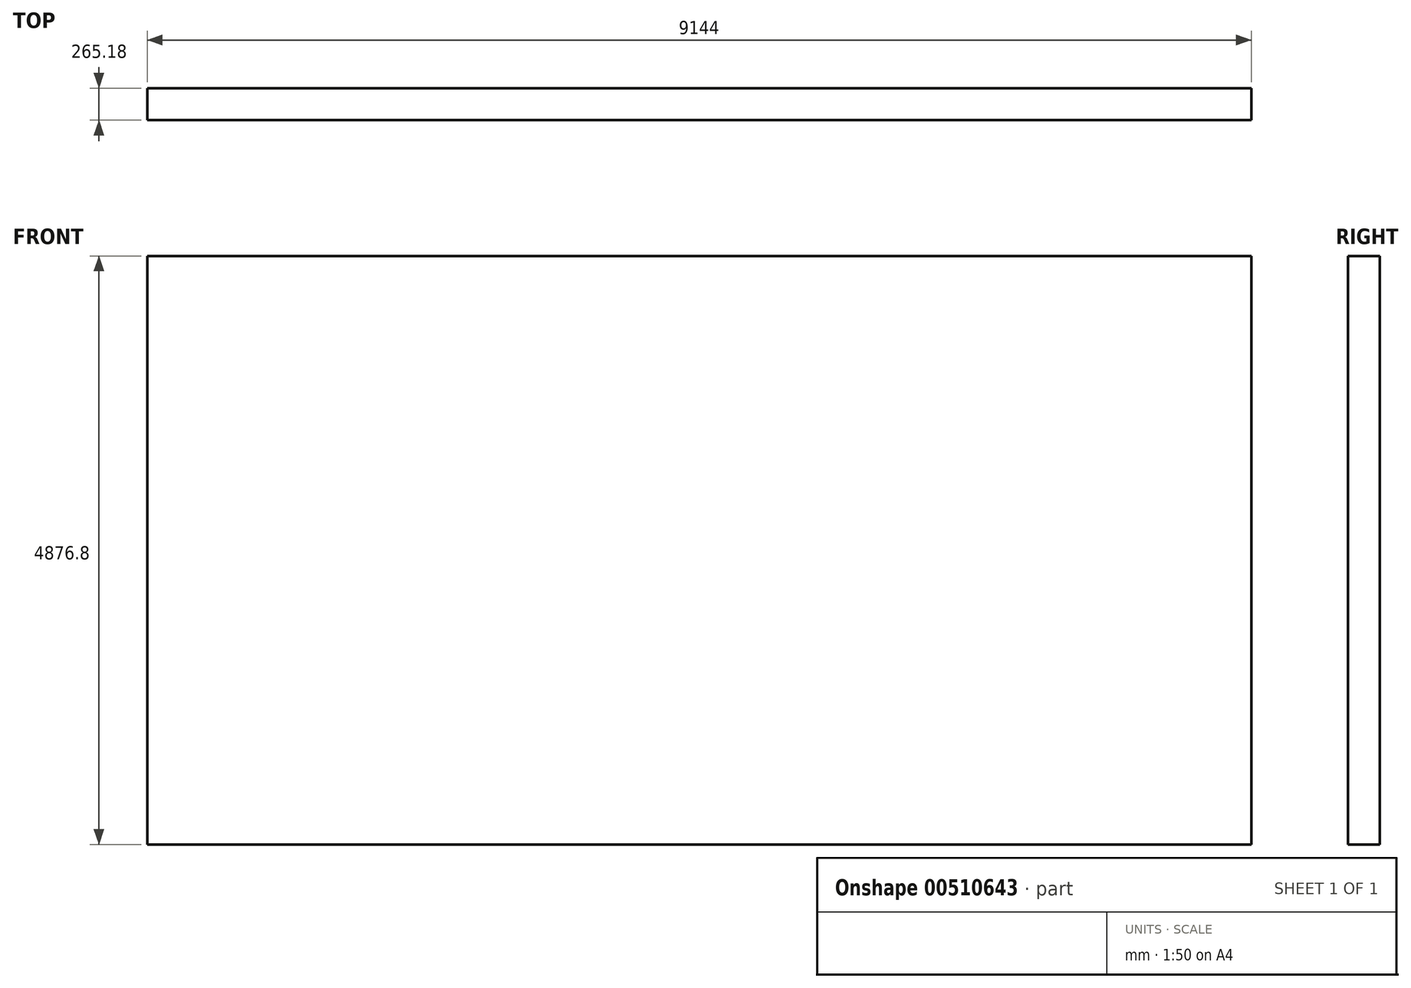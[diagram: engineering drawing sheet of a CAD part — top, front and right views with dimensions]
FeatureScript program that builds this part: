
annotation { "Feature Type Name" : "Feature", "Feature Type Description" : "" }
export const myFeature = defineFeature(function(context is Context, id is Id, definition is map)
    precondition{}
    {
        {
            var Q0;
            Q0=qCreatedBy(makeId("Front.planeOp"),FACE);
            var sketch = newSketch(context, id + "F0", { "sketchPlane" : qUnion([Q0])});
            skLineSegment(sketch, "E0", {"start": v(-4579.52, 3880.9) * mm, "end": v(-4579.52, -995.9) * mm});
            skLineSegment(sketch, "E1", {"start": v(-4579.52, -995.9) * mm, "end": v(4564.48, -995.9) * mm});
            skLineSegment(sketch, "E2", {"start": v(4564.48, -995.9) * mm, "end": v(4564.48, 3880.9) * mm});
            skLineSegment(sketch, "E3", {"start": v(4564.48, 3880.9) * mm, "end": v(-4579.52, 3880.9) * mm});
            skSolve(sketch);
        }
        {
            var Q0;
            Q0 = qSketchRegion(id + "F0", true);
            extrude(context, id + "F1", {"entities" : qUnion([Q0]), "depth" : 265.18 * mm, "offsetDistance" : 30.48 * mm});
        }
    });
